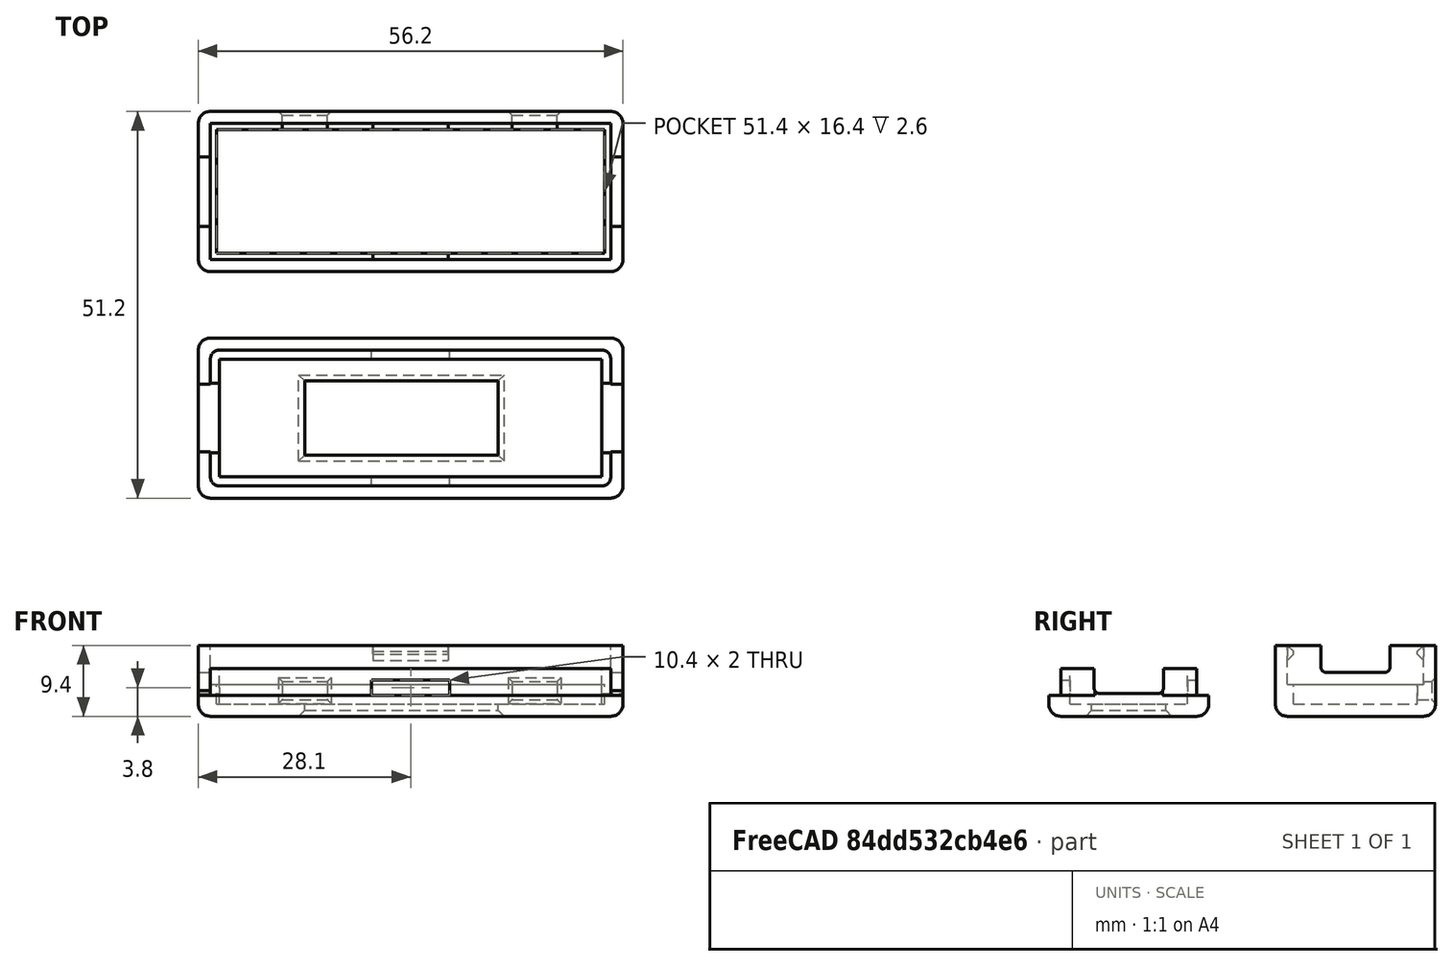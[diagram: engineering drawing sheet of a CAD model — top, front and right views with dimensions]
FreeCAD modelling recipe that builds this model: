
FCSTD DOCUMENT  (FreeCAD 0.16R)
Label: USB-C_Tester_v0.3
License: All rights reserved
LicenseURL: http://en.wikipedia.org/wiki/All_rights_reserved
objects: Part::Box×21, Part::Fillet×7, Part::Cut×6, Part::Chamfer×4, Part::MultiFuse×4
note: 42 computed .brp shape members not serialized (recipe doc carries the construction recipe); baked Part::Feature solids carry a one-line shape summary decoded from their .brp

FEATURE [Part::Box] Box  label="unten_außen"
  Height = 9.4
  Length = 56.2
  Placement = pos=(-1.6,-1.6,0) rot=(0,0,1;0rad)
  Width = 21.2
FEATURE [Part::Box] Box001  label="unten_innen"
  Height = 9.4
  Length = 53
  Placement = pos=(0,0,1.6) rot=(0,0,1;0rad)
  Width = 18
FEATURE [Part::Cut] Cut  label="Schale_roh"
  Base = -> Box
  Tool = -> Box001
FEATURE [Part::Fillet] Fillet  label="Schale_unten"
  Base = -> Cut
  Edges = 8 edges r=1.6: [Edge1,Edge3,Edge4,Edge5,Edge6,Edge14,Edge15,Edge16]
FEATURE [Part::Box] Box002  label="Auflage_außen"
  Height = 2.6
  Length = 53
  Placement = pos=(0,0,1.6) rot=(0,0,1;0rad)
  Width = 18
FEATURE [Part::Box] Box003  label="Auflage_innen"
  Height = 2.6
  Length = 51.4
  Placement = pos=(0.8,0.8,1.6) rot=(0,0,1;0rad)
  Width = 16.4
FEATURE [Part::Cut] Cut001  label="Auflage"
  Base = -> Box002
  Tool = -> Box003
FEATURE [Part::Box] Box004  label="Haken1_roh"
  Height = 2
  Length = 10
  Placement = pos=(21.5,-0.2,7.4) rot=(0,0,1;0rad)
  Width = 1
FEATURE [Part::Chamfer] Chamfer  label="Haken1"
  Base = -> Box004
  Edges = 2 edges r=0.8: [Edge11,Edge12]
FEATURE [Part::Box] Box005  label="Haken2_roh"
  Height = 2
  Length = 10
  Placement = pos=(21.5,17.2,7.4) rot=(0,0,1;0rad)
  Width = 1
FEATURE [Part::Chamfer] Chamfer001  label="Haken2"
  Base = -> Box005
  Edges = 2 edges r=0.8: [Edge9,Edge10]
FEATURE [Part::Box] Box006  label="USB_Buchse1_roh"
  Height = 4
  Length = 10
  Placement = pos=(-5,4.4,5.8) rot=(0,0,1;0rad)
  Width = 9.2
FEATURE [Part::Box] Box008  label="Button1"
  Height = 2.4
  Length = 6
  Placement = pos=(9.5,14,2.2) rot=(0,0,1;0rad)
  Width = 10
FEATURE [Part::Box] Box009  label="Button2"
  Height = 2.4
  Length = 6
  Placement = pos=(39.9,14,2.2) rot=(0,0,1;0rad)
  Width = 10
FEATURE [Part::Box] Box010  label="oben_außen"
  Height = 2.8
  Length = 56.2
  Placement = pos=(-1.6,-31.6,0) rot=(0,0,1;0rad)
  Width = 21.2
FEATURE [Part::Box] Box011  label="oben_innen"
  Height = 9.4
  Length = 53
  Placement = pos=(0,-30,1.6) rot=(0,0,1;0rad)
  Width = 18
FEATURE [Part::Cut] Cut002  label="Schale_oben_roh"
  Base = -> Box010
  Tool = -> Box011
FEATURE [Part::Fillet] Fillet001  label="Schale_oben"
  Base = -> Cut002
  Edges = 8 edges r=1.6: [Edge1,Edge3,Edge4,Edge5,Edge6,Edge14,Edge15,Edge16]
FEATURE [Part::Box] Box012  label="Rahmen_außen"
  Height = 4.7
  Length = 53
  Placement = pos=(0,-30,1.6) rot=(0,0,1;0rad)
  Width = 18
FEATURE [Part::Box] Box013  label="Rahmen_innen"
  Height = 4.8
  Length = 50.6
  Placement = pos=(1.2,-28.8,1.6) rot=(0,0,1;0rad)
  Width = 15.6
FEATURE [Part::Cut] Cut003  label="Rahmen"
  Base = -> Box012
  Tool = -> Box013
FEATURE [Part::Box] Box014  label="OLED"
  Height = 1.6
  Length = 25.6
  Placement = pos=(12.5,-25.9,0) rot=(0,0,1;0rad)
  Width = 9.8
FEATURE [Part::Box] Box017  label="Oese1"
  Height = 2
  Length = 10.4
  Placement = pos=(21.3,-33,2.8) rot=(0,0,1;0rad)
  Width = 5
FEATURE [Part::Box] Box018  label="Oese2"
  Height = 2
  Length = 10.4
  Placement = pos=(21.3,-15,2.8) rot=(0,0,1;0rad)
  Width = 5
FEATURE [Part::Box] Box019  label="USB_Buchse2_roh"
  Height = 4.6
  Length = 10
  Placement = pos=(47,4.4,5.8) rot=(0,0,1;0rad)
  Width = 9.2
FEATURE [Part::Box] Box020  label="USB_Buchse3_roh"
  Height = 4.6
  Length = 10
  Placement = pos=(-5,-25.6,3) rot=(0,0,1;0rad)
  Width = 9.2
FEATURE [Part::Box] Box021  label="USB_Buchse4_roh"
  Height = 4.6
  Length = 10
  Placement = pos=(47,-25.6,3) rot=(0,0,1;0rad)
  Width = 9.2
FEATURE [Part::Fillet] Fillet002  label="USB_Buchse1"
  Base = -> Box006
  Edges = 2 edges r=0.8: [Edge9,Edge11]
FEATURE [Part::Fillet] Fillet003  label="USB_Buchse2"
  Base = -> Box019
  Edges = 2 edges r=0.8: [Edge9,Edge11]
FEATURE [Part::Box] Box022  label="Nut1"
  Height = 3
  Length = 1.6
  Placement = pos=(-1.6,-25.5,2.8) rot=(0,0,1;0rad)
  Width = 9
FEATURE [Part::Box] Box023  label="Nut2"
  Height = 3
  Length = 1.6
  Placement = pos=(53,-25.5,2.8) rot=(0,0,1;0rad)
  Width = 9
FEATURE [Part::Fillet] Fillet004  label="USB-Buchse3"
  Base = -> Box020
  Edges = 2 edges r=0.8: [Edge9,Edge11]
FEATURE [Part::Fillet] Fillet005  label="USB-Buchse4"
  Base = -> Box021
  Edges = 2 edges r=0.8: [Edge9,Edge11]
FEATURE [Part::MultiFuse] Fusion  label="bottom_raw"
  Shapes = -> [Fillet,Cut001,Chamfer,Chamfer001]
FEATURE [Part::MultiFuse] Fusion001  label="bottom_cutouts"
  Shapes = -> [Box008,Box009,Fillet002,Fillet003]
FEATURE [Part::MultiFuse] Fusion002  label="top_raw"
  Shapes = -> [Fillet001,Cut003,Box022,Box023]
FEATURE [Part::MultiFuse] Fusion003  label="top_cutouts"
  Shapes = -> [Box014,Box017,Box018,Fillet004,Fillet005]
FEATURE [Part::Cut] Cut004  label="cover_bottom_raw"
  Base = -> Fusion
  Tool = -> Fusion001
FEATURE [Part::Cut] Cut005  label="cover_top_raw"
  Base = -> Fusion002
  Tool = -> Fusion003
FEATURE [Part::Chamfer] Chamfer002  label="cover_bottom"
  Base = -> Cut004
  Edges = 8 edges r=0.5: [Edge83,Edge84,Edge85,Edge86,Edge87,Edge88,Edge89,Edge90]
FEATURE [Part::Chamfer] Chamfer003  label="cover_top_raw_2"
  Base = -> Cut005
  Edges = 4 edges r=0.8: [Edge71,Edge72,Edge73,Edge74]
FEATURE [Part::Fillet] Fillet006  label="cover_top"
  Base = -> Chamfer003
  Edges = 4 edges r=1.2: [Edge131,Edge135,Edge147,Edge149]
